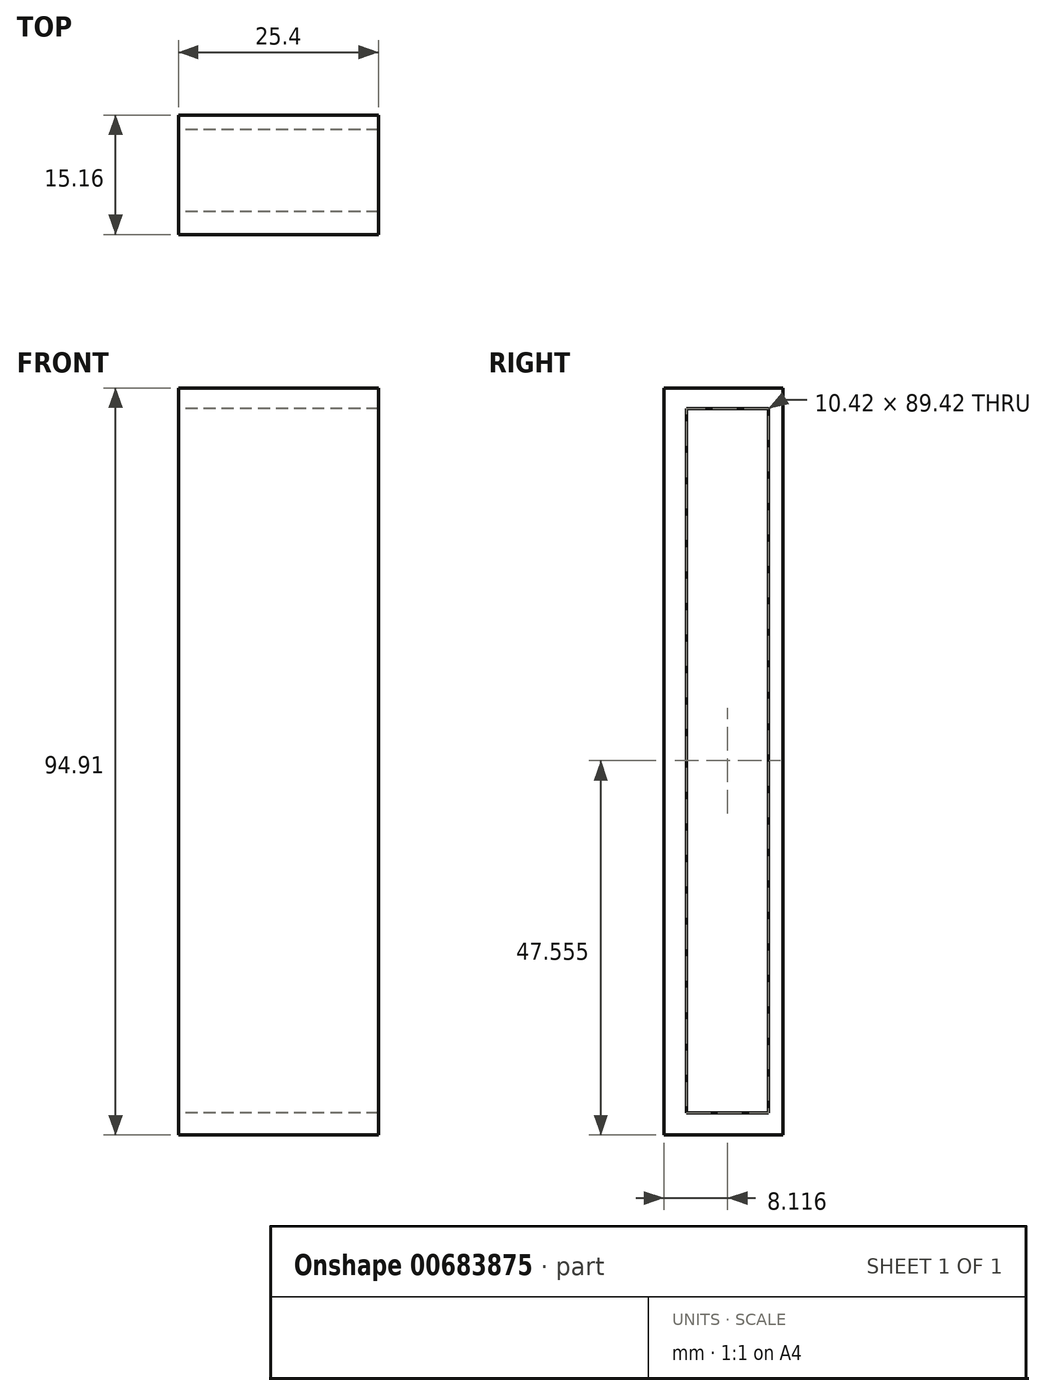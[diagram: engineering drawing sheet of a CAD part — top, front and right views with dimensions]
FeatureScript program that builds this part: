
annotation { "Feature Type Name" : "Feature", "Feature Type Description" : "" }
export const myFeature = defineFeature(function(context is Context, id is Id, definition is map)
    precondition{}
    {
        {
            var Q0;
            Q0=qCreatedBy(makeId("Right.planeOp"),FACE);
            var sketch = newSketch(context, id + "F0", { "sketchPlane" : qUnion([Q0])});
            skLineSegment(sketch, "E0", {"start": v(14.32, 28.67) * mm, "end": v(20.7, 28.67) * mm});
            skLineSegment(sketch, "E1", {"start": v(20.7, 28.67) * mm, "end": v(20.7, 26.03) * mm});
            skLineSegment(sketch, "E2", {"start": v(20.7, 26.03) * mm, "end": v(14.32, 26.03) * mm});
            skLineSegment(sketch, "E3", {"start": v(14.32, 26.03) * mm, "end": v(14.32, 28.67) * mm});
            skLineSegment(sketch, "E4", {"start": v(14.32, -66.24) * mm, "end": v(20.7, -66.24) * mm});
            skLineSegment(sketch, "E5", {"start": v(20.7, -66.24) * mm, "end": v(20.7, -63.4) * mm});
            skLineSegment(sketch, "E6", {"start": v(20.7, -63.4) * mm, "end": v(14.32, -63.4) * mm});
            skLineSegment(sketch, "E7", {"start": v(14.32, -63.4) * mm, "end": v(14.32, -66.24) * mm});
            skLineSegment(sketch, "E8", {"start": v(20.7, 28.67) * mm, "end": v(20.7, 18.78) * mm});
            skLineSegment(sketch, "E9", {"start": v(20.7, 18.78) * mm, "end": v(22.54, 18.78) * mm});
            skLineSegment(sketch, "E10", {"start": v(22.54, 18.78) * mm, "end": v(22.54, 28.67) * mm});
            skLineSegment(sketch, "E11.bottom", {"start": v(20.7, 28.67) * mm, "end": v(22.54, 28.67) * mm});
            skLineSegment(sketch, "E11.right", {"start": v(22.54, 28.67) * mm, "end": v(22.54, 18.78) * mm});
            skLineSegment(sketch, "E12.top", {"start": v(20.7, 9.42) * mm, "end": v(22.54, 9.42) * mm});
            skLineSegment(sketch, "E12.left", {"start": v(20.7, 18.78) * mm, "end": v(20.7, 9.42) * mm});
            skLineSegment(sketch, "E12.right", {"start": v(22.54, 18.78) * mm, "end": v(22.54, 9.42) * mm});
            skLineSegment(sketch, "E13.top", {"start": v(20.7, 0.97) * mm, "end": v(22.54, 0.97) * mm});
            skLineSegment(sketch, "E13.left", {"start": v(20.7, 9.42) * mm, "end": v(20.7, 0.97) * mm});
            skLineSegment(sketch, "E13.right", {"start": v(22.54, 9.42) * mm, "end": v(22.54, 0.97) * mm});
            skLineSegment(sketch, "E14.top", {"start": v(20.7, -8.17) * mm, "end": v(22.54, -8.17) * mm});
            skLineSegment(sketch, "E14.left", {"start": v(20.7, 0.97) * mm, "end": v(20.7, -8.17) * mm});
            skLineSegment(sketch, "E14.right", {"start": v(22.54, 0.97) * mm, "end": v(22.54, -8.17) * mm});
            skLineSegment(sketch, "E15.top", {"start": v(20.7, -18.3) * mm, "end": v(22.54, -18.3) * mm});
            skLineSegment(sketch, "E15.left", {"start": v(20.7, -8.17) * mm, "end": v(20.7, -18.3) * mm});
            skLineSegment(sketch, "E15.right", {"start": v(22.54, -8.17) * mm, "end": v(22.54, -18.3) * mm});
            skLineSegment(sketch, "E16.top", {"start": v(20.7, -26.95) * mm, "end": v(22.54, -26.95) * mm});
            skLineSegment(sketch, "E16.left", {"start": v(20.7, -18.3) * mm, "end": v(20.7, -26.95) * mm});
            skLineSegment(sketch, "E16.right", {"start": v(22.54, -18.3) * mm, "end": v(22.54, -26.95) * mm});
            skLineSegment(sketch, "E17.top", {"start": v(20.7, -39.15) * mm, "end": v(22.54, -39.15) * mm});
            skLineSegment(sketch, "E17.left", {"start": v(20.7, -26.95) * mm, "end": v(20.7, -39.15) * mm});
            skLineSegment(sketch, "E17.right", {"start": v(22.54, -26.95) * mm, "end": v(22.54, -39.15) * mm});
            skLineSegment(sketch, "E18.top", {"start": v(20.7, -48.14) * mm, "end": v(22.54, -48.14) * mm});
            skLineSegment(sketch, "E18.left", {"start": v(20.7, -39.15) * mm, "end": v(20.7, -48.14) * mm});
            skLineSegment(sketch, "E18.right", {"start": v(22.54, -39.15) * mm, "end": v(22.54, -48.14) * mm});
            skLineSegment(sketch, "E19.top", {"start": v(20.7, -57.47) * mm, "end": v(22.54, -57.47) * mm});
            skLineSegment(sketch, "E19.left", {"start": v(20.7, -48.14) * mm, "end": v(20.7, -57.47) * mm});
            skLineSegment(sketch, "E19.right", {"start": v(22.54, -48.14) * mm, "end": v(22.54, -57.47) * mm});
            skLineSegment(sketch, "E20.top", {"start": v(20.7, -66.24) * mm, "end": v(22.54, -66.24) * mm});
            skLineSegment(sketch, "E20.left", {"start": v(20.7, -57.47) * mm, "end": v(20.7, -66.24) * mm});
            skLineSegment(sketch, "E20.right", {"start": v(22.54, -57.47) * mm, "end": v(22.54, -66.24) * mm});
            skLineSegment(sketch, "E21.bottom", {"start": v(14.32, 26.03) * mm, "end": v(10.29, 26.03) * mm});
            skLineSegment(sketch, "E21.top", {"start": v(14.32, 28.67) * mm, "end": v(10.29, 28.67) * mm});
            skLineSegment(sketch, "E21.right", {"start": v(10.29, 26.03) * mm, "end": v(10.29, 28.67) * mm});
            skPoint(sketch, "E22.oppositeSnap0", {"position": v(17.51, -63.4) * mm});
            skLineSegment(sketch, "E22.bottom", {"start": v(14.32, -66.24) * mm, "end": v(10.29, -66.24) * mm});
            skLineSegment(sketch, "E22.top", {"start": v(14.32, -63.4) * mm, "end": v(10.29, -63.4) * mm});
            skLineSegment(sketch, "E22.left", {"start": v(14.32, -66.24) * mm, "end": v(14.32, -63.4) * mm});
            skLineSegment(sketch, "E22.right", {"start": v(10.29, -66.24) * mm, "end": v(10.29, -63.4) * mm});
            skLineSegment(sketch, "E23.bottom", {"start": v(10.29, 28.67) * mm, "end": v(7.38, 28.67) * mm});
            skLineSegment(sketch, "E23.top", {"start": v(10.29, 23.67) * mm, "end": v(7.38, 23.67) * mm});
            skLineSegment(sketch, "E23.left", {"start": v(10.29, 28.67) * mm, "end": v(10.29, 23.67) * mm});
            skLineSegment(sketch, "E23.right", {"start": v(7.38, 28.67) * mm, "end": v(7.38, 23.67) * mm});
            skLineSegment(sketch, "E24.bottom", {"start": v(7.38, 23.67) * mm, "end": v(10.29, 23.67) * mm});
            skLineSegment(sketch, "E24.top", {"start": v(7.38, 18.82) * mm, "end": v(10.29, 18.82) * mm});
            skLineSegment(sketch, "E24.left", {"start": v(7.38, 23.67) * mm, "end": v(7.38, 18.82) * mm});
            skLineSegment(sketch, "E24.right", {"start": v(10.29, 23.67) * mm, "end": v(10.29, 18.82) * mm});
            skLineSegment(sketch, "E25.bottom", {"start": v(10.29, 18.82) * mm, "end": v(7.38, 18.82) * mm});
            skLineSegment(sketch, "E25.top", {"start": v(10.29, 14.3) * mm, "end": v(7.38, 14.3) * mm});
            skLineSegment(sketch, "E25.left", {"start": v(10.29, 18.82) * mm, "end": v(10.29, 14.3) * mm});
            skLineSegment(sketch, "E25.right", {"start": v(7.38, 18.82) * mm, "end": v(7.38, 14.3) * mm});
            skLineSegment(sketch, "E26.bottom", {"start": v(7.38, 14.3) * mm, "end": v(10.29, 14.3) * mm});
            skLineSegment(sketch, "E26.top", {"start": v(7.38, 9.63) * mm, "end": v(10.29, 9.63) * mm});
            skLineSegment(sketch, "E26.left", {"start": v(7.38, 14.3) * mm, "end": v(7.38, 9.63) * mm});
            skLineSegment(sketch, "E26.right", {"start": v(10.29, 14.3) * mm, "end": v(10.29, 9.63) * mm});
            skLineSegment(sketch, "E27.bottom", {"start": v(10.29, 9.63) * mm, "end": v(7.38, 9.63) * mm});
            skLineSegment(sketch, "E27.top", {"start": v(10.29, 4.45) * mm, "end": v(7.38, 4.45) * mm});
            skLineSegment(sketch, "E27.left", {"start": v(10.29, 9.63) * mm, "end": v(10.29, 4.45) * mm});
            skLineSegment(sketch, "E27.right", {"start": v(7.38, 9.63) * mm, "end": v(7.38, 4.45) * mm});
            skLineSegment(sketch, "E28.bottom", {"start": v(7.38, 4.45) * mm, "end": v(10.29, 4.45) * mm});
            skLineSegment(sketch, "E28.top", {"start": v(7.38, 0) * mm, "end": v(10.29, 0) * mm});
            skLineSegment(sketch, "E28.left", {"start": v(7.38, 4.45) * mm, "end": v(7.38, 0) * mm});
            skLineSegment(sketch, "E28.right", {"start": v(10.29, 4.45) * mm, "end": v(10.29, 0) * mm});
            skLineSegment(sketch, "E29.top", {"start": v(7.38, -5.08) * mm, "end": v(10.29, -5.08) * mm});
            skLineSegment(sketch, "E29.left", {"start": v(7.38, 0) * mm, "end": v(7.38, -5.08) * mm});
            skLineSegment(sketch, "E29.right", {"start": v(10.29, 0) * mm, "end": v(10.29, -5.08) * mm});
            skLineSegment(sketch, "E30.bottom", {"start": v(10.29, -5.08) * mm, "end": v(7.38, -5.08) * mm});
            skLineSegment(sketch, "E30.top", {"start": v(10.29, -9.76) * mm, "end": v(7.38, -9.76) * mm});
            skLineSegment(sketch, "E30.left", {"start": v(10.29, -5.08) * mm, "end": v(10.29, -9.76) * mm});
            skLineSegment(sketch, "E30.right", {"start": v(7.38, -5.08) * mm, "end": v(7.38, -9.76) * mm});
            skLineSegment(sketch, "E31.bottom", {"start": v(7.38, -9.76) * mm, "end": v(10.29, -9.76) * mm});
            skLineSegment(sketch, "E31.top", {"start": v(7.38, -14.1) * mm, "end": v(10.29, -14.1) * mm});
            skLineSegment(sketch, "E31.left", {"start": v(7.38, -9.76) * mm, "end": v(7.38, -14.1) * mm});
            skLineSegment(sketch, "E31.right", {"start": v(10.29, -9.76) * mm, "end": v(10.29, -14.1) * mm});
            skLineSegment(sketch, "E32.bottom", {"start": v(10.29, -14.1) * mm, "end": v(7.38, -14.1) * mm});
            skLineSegment(sketch, "E32.top", {"start": v(10.29, -18.95) * mm, "end": v(7.38, -18.95) * mm});
            skLineSegment(sketch, "E32.left", {"start": v(10.29, -14.1) * mm, "end": v(10.29, -18.95) * mm});
            skLineSegment(sketch, "E32.right", {"start": v(7.38, -14.1) * mm, "end": v(7.38, -18.95) * mm});
            skLineSegment(sketch, "E33.bottom", {"start": v(7.38, -18.95) * mm, "end": v(10.29, -18.95) * mm});
            skLineSegment(sketch, "E33.top", {"start": v(7.38, -22.63) * mm, "end": v(10.29, -22.63) * mm});
            skLineSegment(sketch, "E33.left", {"start": v(7.38, -18.95) * mm, "end": v(7.38, -22.63) * mm});
            skLineSegment(sketch, "E33.right", {"start": v(10.29, -18.95) * mm, "end": v(10.29, -22.63) * mm});
            skLineSegment(sketch, "E34.bottom", {"start": v(10.29, -22.63) * mm, "end": v(7.38, -22.63) * mm});
            skLineSegment(sketch, "E34.top", {"start": v(10.29, -27.48) * mm, "end": v(7.38, -27.48) * mm});
            skLineSegment(sketch, "E34.left", {"start": v(10.29, -22.63) * mm, "end": v(10.29, -27.48) * mm});
            skLineSegment(sketch, "E34.right", {"start": v(7.38, -22.63) * mm, "end": v(7.38, -27.48) * mm});
            skLineSegment(sketch, "E35.bottom", {"start": v(7.38, -27.48) * mm, "end": v(10.29, -27.48) * mm});
            skLineSegment(sketch, "E35.top", {"start": v(7.38, -32.16) * mm, "end": v(10.29, -32.16) * mm});
            skLineSegment(sketch, "E35.left", {"start": v(7.38, -27.48) * mm, "end": v(7.38, -32.16) * mm});
            skLineSegment(sketch, "E35.right", {"start": v(10.29, -27.48) * mm, "end": v(10.29, -32.16) * mm});
            skLineSegment(sketch, "E36.bottom", {"start": v(10.29, -32.16) * mm, "end": v(7.38, -32.16) * mm});
            skLineSegment(sketch, "E36.top", {"start": v(10.29, -36.5) * mm, "end": v(7.38, -36.5) * mm});
            skLineSegment(sketch, "E36.left", {"start": v(10.29, -32.16) * mm, "end": v(10.29, -36.5) * mm});
            skLineSegment(sketch, "E36.right", {"start": v(7.38, -32.16) * mm, "end": v(7.38, -36.5) * mm});
            skLineSegment(sketch, "E37.bottom", {"start": v(7.38, -36.5) * mm, "end": v(10.29, -36.5) * mm});
            skLineSegment(sketch, "E37.top", {"start": v(7.38, -40.68) * mm, "end": v(10.29, -40.68) * mm});
            skLineSegment(sketch, "E37.left", {"start": v(7.38, -36.5) * mm, "end": v(7.38, -40.68) * mm});
            skLineSegment(sketch, "E37.right", {"start": v(10.29, -36.5) * mm, "end": v(10.29, -40.68) * mm});
            skLineSegment(sketch, "E38.bottom", {"start": v(10.29, -40.68) * mm, "end": v(7.38, -40.68) * mm});
            skLineSegment(sketch, "E38.top", {"start": v(10.29, -45.36) * mm, "end": v(7.38, -45.36) * mm});
            skLineSegment(sketch, "E38.left", {"start": v(10.29, -40.68) * mm, "end": v(10.29, -45.36) * mm});
            skLineSegment(sketch, "E38.right", {"start": v(7.38, -40.68) * mm, "end": v(7.38, -45.36) * mm});
            skLineSegment(sketch, "E39.bottom", {"start": v(7.38, -45.36) * mm, "end": v(10.29, -45.36) * mm});
            skLineSegment(sketch, "E39.top", {"start": v(7.38, -49.87) * mm, "end": v(10.29, -49.87) * mm});
            skLineSegment(sketch, "E39.left", {"start": v(7.38, -45.36) * mm, "end": v(7.38, -49.87) * mm});
            skLineSegment(sketch, "E39.right", {"start": v(10.29, -45.36) * mm, "end": v(10.29, -49.87) * mm});
            skLineSegment(sketch, "E40.bottom", {"start": v(10.29, -49.87) * mm, "end": v(7.38, -49.87) * mm});
            skLineSegment(sketch, "E40.top", {"start": v(10.29, -54.72) * mm, "end": v(7.38, -54.72) * mm});
            skLineSegment(sketch, "E40.left", {"start": v(10.29, -49.87) * mm, "end": v(10.29, -54.72) * mm});
            skLineSegment(sketch, "E40.right", {"start": v(7.38, -49.87) * mm, "end": v(7.38, -54.72) * mm});
            skLineSegment(sketch, "E41.bottom", {"start": v(7.38, -54.72) * mm, "end": v(10.29, -54.72) * mm});
            skLineSegment(sketch, "E41.top", {"start": v(7.38, -58.9) * mm, "end": v(10.29, -58.9) * mm});
            skLineSegment(sketch, "E41.left", {"start": v(7.38, -54.72) * mm, "end": v(7.38, -58.9) * mm});
            skLineSegment(sketch, "E41.right", {"start": v(10.29, -54.72) * mm, "end": v(10.29, -58.9) * mm});
            skLineSegment(sketch, "E42.bottom", {"start": v(10.29, -58.9) * mm, "end": v(7.38, -58.9) * mm});
            skLineSegment(sketch, "E42.top", {"start": v(10.29, -62.07) * mm, "end": v(7.38, -62.07) * mm});
            skLineSegment(sketch, "E42.left", {"start": v(10.29, -58.9) * mm, "end": v(10.29, -62.07) * mm});
            skLineSegment(sketch, "E42.right", {"start": v(7.38, -58.9) * mm, "end": v(7.38, -62.07) * mm});
            skLineSegment(sketch, "E43.bottom", {"start": v(7.38, -62.07) * mm, "end": v(10.29, -62.07) * mm});
            skLineSegment(sketch, "E43.top", {"start": v(7.38, -66.24) * mm, "end": v(10.29, -66.24) * mm});
            skLineSegment(sketch, "E43.left", {"start": v(7.38, -62.07) * mm, "end": v(7.38, -66.24) * mm});
            skLineSegment(sketch, "E43.right", {"start": v(10.29, -62.07) * mm, "end": v(10.29, -66.24) * mm});
            skSolve(sketch);
        }
        {
            var Q0;
            Q0 = qSketchRegion(id + "F0", true);
            extrude(context, id + "F1", {"entities" : qUnion([Q0]), "depth" : 25.4 * mm, "offsetDistance" : 25.4 * mm});
        }
    });
